# Revit family: Genie_Site_ArticulatingBoom_Z51_1
name_source: partatom
category: Site
revit_build: Autodesk Revit 2017 (Build: 20160225_1515(x64)
units: mm (PartAtom-declared; Revit-internal decimal feet)

## family parameters
Always vertical = Yes
Cut with Voids When Loaded = No
OmniClass Number = 23.50.85.17
OmniClass Title = Telescoping Platforms
Part Type = Normal
Round Connector Dimension = Use Diameter
Shared = No
Work Plane-Based = No

## types (1)
- Z51
    Assembly Code = E1030900
    AssetType = Fixed
    BIMObjectName = Genie_Site_ArticulatingBoom_Z51
    ClassificationName = Uniclass2015
    ClassificationValue = Pr_65_80_47_95
    Color = Grey & Blue
    Cost = 0 $
    Description = The Genie® Z®-51/30J RT articulating boom lift provides lifting versatility with a combination of up, out and over positioning capabilities with outreach that’s second to none. Ideal for outdoor construction and industrial applications, this model's tight turning radius and zero tailswing make for easy manoeuvring in confined work areas.
    DocumentationLiterature = http://genielift.com.au
    DocumentationTechnical = http://genielift.com.au
    DurationUnit = Years
    ExpectedLife = 0
    Features = Full-time active oscillating axle helps maintain traction on rough terrain. 4WD and 45% gradeability for superior terrainability. Dual parallelogram and fully proportional controls for precise boom positioning and smooth performance. 1.52 m (5 ft) articulating jib with a 135° vertical rotation to accurately position workers. 160° hydraulic platform rotation and self-levelling platform for precise platform positioning and easy operation.
    Finish = Painted Steel
    IfcExportAs = IfcTransportElement
    IfcExportType = IfcTransportElementType
    Keynote = X
    Manufacturer = Genie
    ManufacturerName = Genie
    Material = Painted Steel
    Model = Genie - Articulating Boom
    ModelNumber = Z51
    ModelReference = Genie - Articulating Boom
    NBSDescription = Vertical lifting platforms
    NBSObjectName = Genie - Vertical lifting platforms
    NBSReference = 90-80-65/350
    NominalDepth = 2290 mm  [stored 7.51312 ft]
    NominalHeight = 2130 mm  [stored 6.98819 ft]
    NominalLength = 7580 mm
    ProductionYear = 2018
    ReplacementCost = 0
    Size = 2.29m x 2.13m x 7.58m
    Type Comments = Z51
    TypeName = Genie - Articulating Boom
    URL = http://www.genielift.co.uk
    WarrantyDurationLabor = 0
    WarrantyDurationParts = 0
    WarrantyDurationUnit = Years
    WarrantyGuarantorLabor = http://www.genielift.co.uk
    WarrantyGuarantorParts = http://www.genielift.co.uk
    _BSBibleVersion = 15
    _BimSpecGuid = 0
    _CurrentRevision = 1
    _DistributedBy = www.bimstore.co.uk

note: [stored X ft] marks values corroborated as IEEE doubles in the binary element streams (Revit-internal decimal feet)

## geometry (parser evidence)
native form markers: Sweep x48
no freeform markers — native parametric forms only
